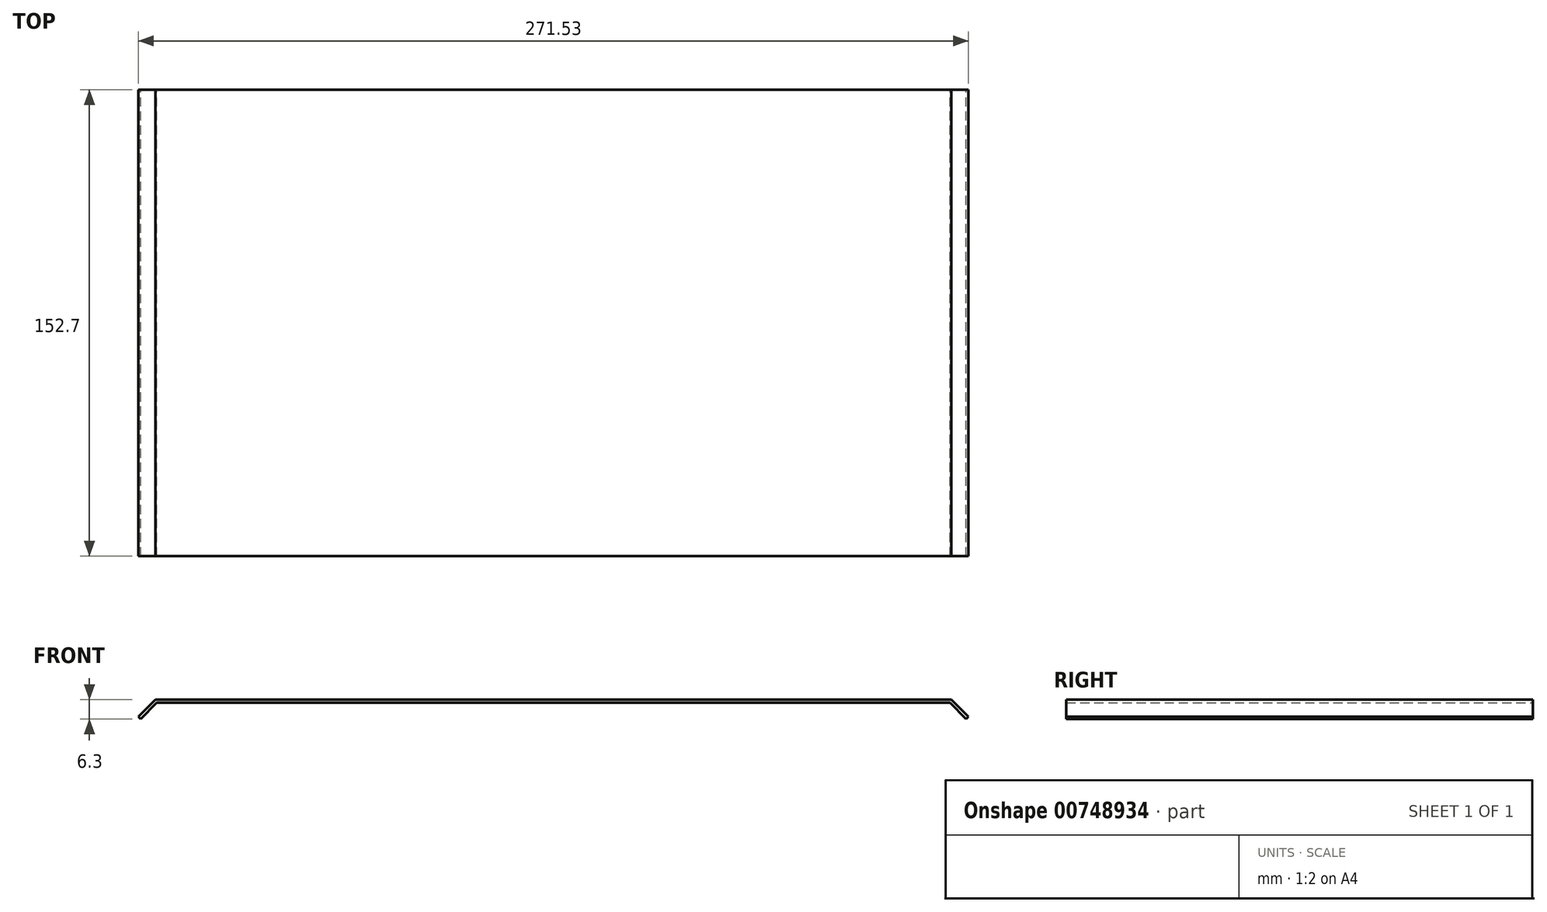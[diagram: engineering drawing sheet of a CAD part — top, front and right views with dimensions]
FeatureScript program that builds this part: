
annotation { "Feature Type Name" : "Feature", "Feature Type Description" : "" }
export const myFeature = defineFeature(function(context is Context, id is Id, definition is map)
    precondition{}
    {
        {
            var Q0;
            Q0=qCreatedBy(makeId("Front.planeOp"),FACE);
            var sketch = newSketch(context, id + "F0", { "sketchPlane" : qUnion([Q0])});
            skLineSegment(sketch, "E0.top", {"start": v(-262.73, -6.4) * mm, "end": v(-3.22, -6.4) * mm});
            skPoint(sketch, "E0.middle", {"position": v(0, 0) * mm});
            skLineSegment(sketch, "E1", {"start": v(-268.03, -11.7) * mm, "end": v(-262.73, -6.4) * mm});
            skLineSegment(sketch, "E2", {"start": v(-132.98, -1.06) * mm, "end": v(-132.98, -0.39) * mm});
            skLineSegment(sketch, "E3.MirrorCS", {"start": v(2.08, -11.7) * mm, "end": v(-3.22, -6.4) * mm});
            skLineSegment(sketch, "E4.0", {"start": v(-263.14, -5.4) * mm, "end": v(-2.8, -5.4) * mm});
            skLineSegment(sketch, "E5", {"start": v(2.08, -11.7) * mm, "end": v(2.79, -11) * mm});
            skLineSegment(sketch, "E6", {"start": v(2.79, -11) * mm, "end": v(-2.8, -5.4) * mm});
            skLineSegment(sketch, "E7", {"start": v(-268.03, -11.7) * mm, "end": v(-268.74, -11) * mm});
            skLineSegment(sketch, "E8", {"start": v(-268.74, -11) * mm, "end": v(-263.14, -5.4) * mm});
            skLineSegment(sketch, "E9.trimOffspring", {"start": v(-262.73, -4.99) * mm, "end": v(-262.73, -1.11) * mm});
            skSolve(sketch);
        }
        {
            var Q0;
            Q0=makeQuery(id+"F0.imprint","IMPRINT",FACE,{"disambiguationData":[TD([[makeQuery(id+"F0.imprint","IMPRINT",EDGE,{"derivedFrom":sQuery(id+"F0.wireOp",EDGE,"E0.top")}),1.0]])]});
            extrude(context, id + "F1", {"entities" : qUnion([Q0]), "depth" : 152.7 * mm, "offsetDistance" : 25 * mm, "symmetric" : true});
        }
    });
